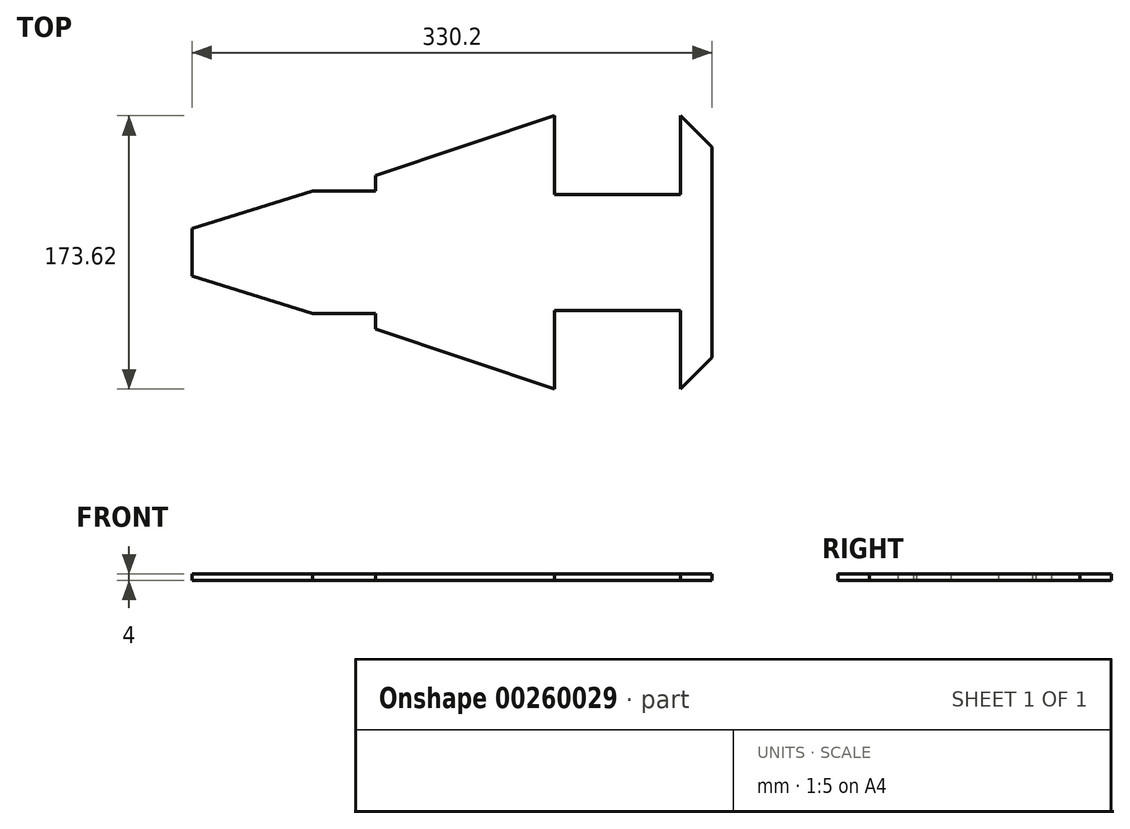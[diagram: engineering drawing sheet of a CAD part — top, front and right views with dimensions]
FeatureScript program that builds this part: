
annotation { "Feature Type Name" : "Feature", "Feature Type Description" : "" }
export const myFeature = defineFeature(function(context is Context, id is Id, definition is map)
    precondition{}
    {
        {
            var Q0;
            Q0=qCreatedBy(makeId("Top.planeOp"),FACE);
            var sketch = newSketch(context, id + "F0", { "sketchPlane" : qUnion([Q0])});
            skLineSegment(sketch, "E0", {"start": v(0, 0) * mm, "end": v(0, 15) * mm});
            skLineSegment(sketch, "E1", {"start": v(76.36, 38.86) * mm, "end": v(116.36, 38.86) * mm});
            skLineSegment(sketch, "E2", {"start": v(116.36, 38.86) * mm, "end": v(116.36, 48.86) * mm});
            skLineSegment(sketch, "E3", {"start": v(0, 15) * mm, "end": v(76.36, 38.86) * mm});
            skLineSegment(sketch, "E4", {"start": v(116.36, 48.86) * mm, "end": v(230.2, 86.8) * mm});
            skLineSegment(sketch, "E5", {"start": v(230.2, 86.8) * mm, "end": v(230.2, 36.8) * mm});
            skLineSegment(sketch, "E6", {"start": v(230.2, 36.8) * mm, "end": v(310.2, 36.8) * mm});
            skLineSegment(sketch, "E7", {"start": v(310.2, 36.8) * mm, "end": v(310.2, 86.8) * mm});
            skLineSegment(sketch, "E8", {"start": v(310.2, 86.8) * mm, "end": v(330.2, 66.8) * mm});
            skPoint(sketch, "E9.end.orphan", {"position": v(330.2, 0.8) * mm});
            skPoint(sketch, "E10.end.orphan", {"position": v(330.2, 0) * mm});
            skLineSegment(sketch, "E11", {"start": v(330.2, 66.8) * mm, "end": v(330.2, 0) * mm});
            skLineSegment(sketch, "E12", {"start": v(0, 0) * mm, "end": v(330.2, 0) * mm});
            skLineSegment(sketch, "E13.MirrorCS", {"start": v(116.36, -38.86) * mm, "end": v(116.36, -48.86) * mm});
            skPoint(sketch, "E14.MirrorP", {"position": v(330.2, -0.8) * mm});
            skLineSegment(sketch, "E15.MirrorCS", {"start": v(76.36, -38.86) * mm, "end": v(116.36, -38.86) * mm});
            skLineSegment(sketch, "E16.MirrorCS", {"start": v(0, -15) * mm, "end": v(76.36, -38.86) * mm});
            skLineSegment(sketch, "E17.MirrorCS", {"start": v(116.36, -48.86) * mm, "end": v(230.2, -86.8) * mm});
            skLineSegment(sketch, "E18.MirrorCS", {"start": v(230.2, -86.8) * mm, "end": v(230.2, -36.8) * mm});
            skLineSegment(sketch, "E19.MirrorCS", {"start": v(230.2, -36.8) * mm, "end": v(310.2, -36.8) * mm});
            skLineSegment(sketch, "E20.MirrorCS", {"start": v(310.2, -36.8) * mm, "end": v(310.2, -86.8) * mm});
            skLineSegment(sketch, "E21.MirrorCS", {"start": v(310.2, -86.8) * mm, "end": v(330.2, -66.8) * mm});
            skLineSegment(sketch, "E22.MirrorCS", {"start": v(330.2, -66.8) * mm, "end": v(330.2, 0) * mm});
            skLineSegment(sketch, "E23.MirrorCS", {"start": v(0, 0) * mm, "end": v(0, -15) * mm});
            skSolve(sketch);
        }
        {
            var Q0;
            Q0=makeQuery(id+"F0.imprint","IMPRINT",FACE,{"disambiguationData":[TD([[makeQuery(id+"F0.imprint","IMPRINT",EDGE,{"derivedFrom":sQuery(id+"F0.wireOp",EDGE,"E0")}),-1.0]])]});
            var Q1;
            Q1=makeQuery(id+"F0.imprint","IMPRINT",FACE,{"disambiguationData":[TD([[makeQuery(id+"F0.imprint","IMPRINT",EDGE,{"derivedFrom":sQuery(id+"F0.wireOp",EDGE,"E12")}),-1.0]])]});
            extrude(context, id + "F1", {"entities" : qUnion([Q0, Q1]), "endBound" : BoundingType.SYMMETRIC, "depth" : 4 * mm});
        }
    });
